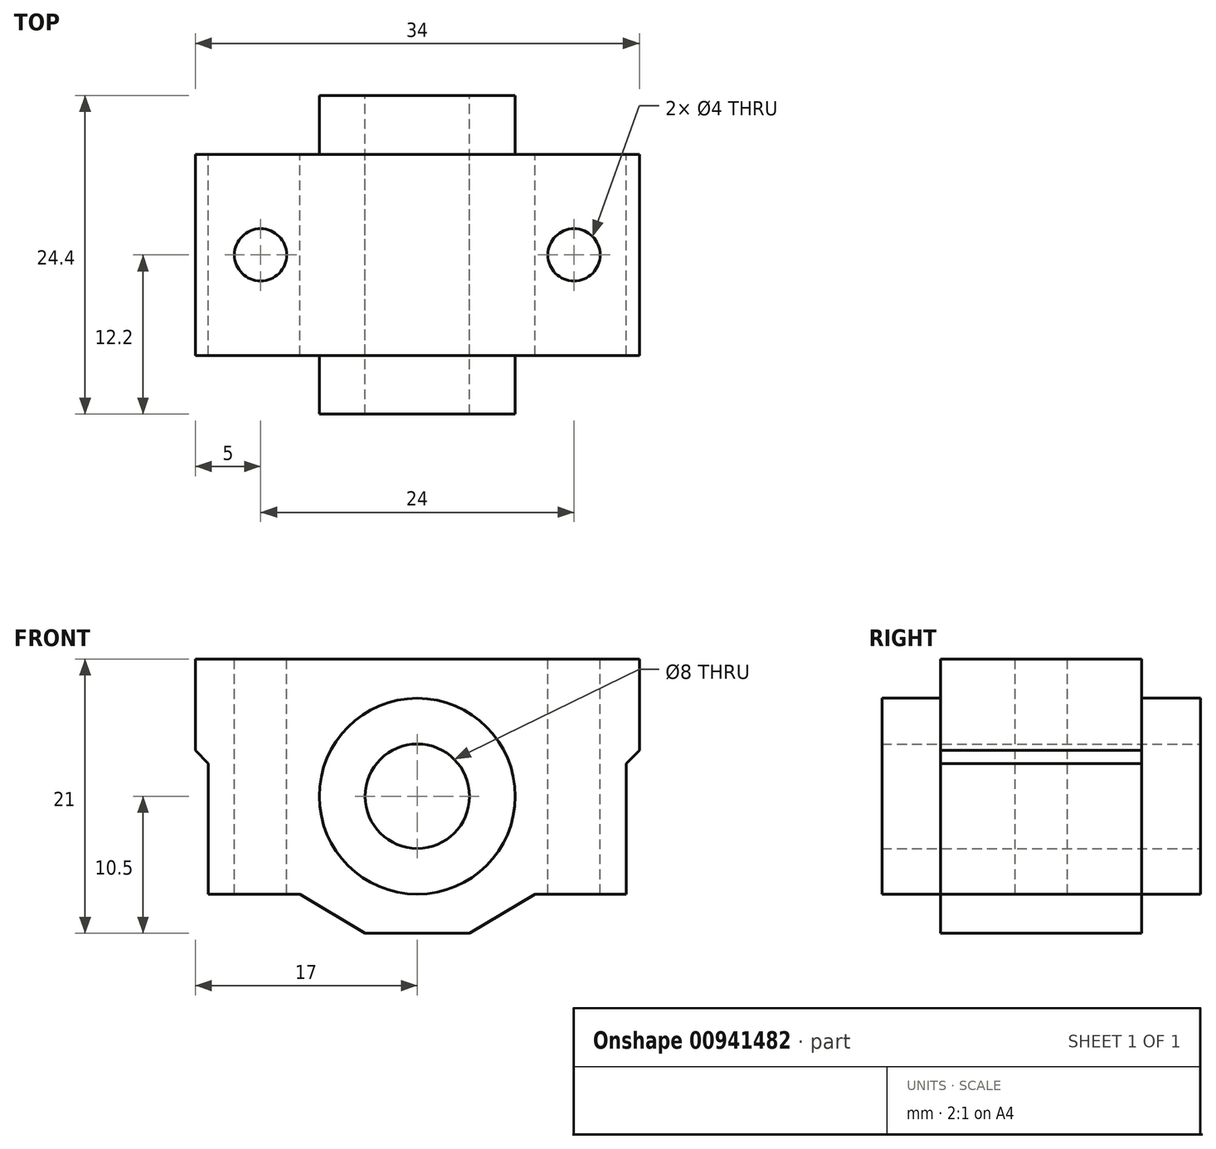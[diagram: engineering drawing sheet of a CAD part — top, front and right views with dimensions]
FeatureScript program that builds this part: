
annotation { "Feature Type Name" : "Feature", "Feature Type Description" : "" }
export const myFeature = defineFeature(function(context is Context, id is Id, definition is map)
    precondition{}
    {
        {
            var Q0;
            Q0=qCreatedBy(makeId("Front.planeOp"),FACE);
            var sketch = newSketch(context, id + "F0", { "sketchPlane" : qUnion([Q0])});
            skLineSegment(sketch, "E0.bottom", {"start": v(4, -10.5) * mm, "end": v(-4, -10.5) * mm});
            skLineSegment(sketch, "E0.top", {"start": v(17, 10.5) * mm, "end": v(-17, 10.5) * mm});
            skLineSegment(sketch, "E0.left", {"start": v(17, 3.5) * mm, "end": v(17, 10.5) * mm});
            skLineSegment(sketch, "E0.right", {"start": v(-17, 3.5) * mm, "end": v(-17, 10.5) * mm});
            skPoint(sketch, "E0.middle", {"position": v(0, 0) * mm});
            skCircle(sketch, "E1", {"center": v(0, 0) * mm, "radius": 7.5 * mm});
            skCircle(sketch, "E2", {"center": v(0, 0) * mm, "radius": 4 * mm});
            skLineSegment(sketch, "E3", {"start": v(16, -7.5) * mm, "end": v(9, -7.5) * mm});
            skLineSegment(sketch, "E4", {"start": v(9, -7.5) * mm, "end": v(4, -10.5) * mm});
            skLineSegment(sketch, "E5", {"start": v(-4, -10.5) * mm, "end": v(-9, -7.5) * mm});
            skLineSegment(sketch, "E6", {"start": v(-9, -7.5) * mm, "end": v(-16, -7.5) * mm});
            skPoint(sketch, "E7.orphan", {"position": v(-17, -10.5) * mm});
            skPoint(sketch, "E8.orphan", {"position": v(17, -10.5) * mm});
            skLineSegment(sketch, "E9", {"start": v(17, 3.5) * mm, "end": v(16, 2.5) * mm});
            skLineSegment(sketch, "E10", {"start": v(16, 2.5) * mm, "end": v(16, -7.5) * mm});
            skLineSegment(sketch, "E11", {"start": v(-17, 3.5) * mm, "end": v(-16, 2.5) * mm});
            skLineSegment(sketch, "E12", {"start": v(-16, 2.5) * mm, "end": v(-16, -7.5) * mm});
            skPoint(sketch, "E13.orphan", {"position": v(-17, -7.5) * mm});
            skPoint(sketch, "E14.orphan", {"position": v(17, -7.5) * mm});
            skSolve(sketch);
        }
        {
            var Q0;
            Q0=makeQuery(id+"F0.imprint","IMPRINT",FACE,{"disambiguationData":[TD([[makeQuery(id+"F0.imprint","IMPRINT",EDGE,{"derivedFrom":sQuery(id+"F0.wireOp",EDGE,"E0.top")}),1.0]])]});
            extrude(context, id + "F1", {"entities" : qUnion([Q0]), "depth" : 7.7 * mm, "offsetDistance" : 25 * mm, "hasSecondDirection" : true, "secondDirectionOppositeDirection" : true, "secondDirectionDepth" : 7.7 * mm});
        }
        {
            var Q0;
            Q0=makeQuery(id+"F1.opExtrude","SWEPT_FACE",FACE,{"disambiguationData":[OSD([sQuery(id+"F0.wireOp",EDGE,"E0.top")])]});
            var sketch = newSketch(context, id + "F2", { "sketchPlane" : qUnion([Q0])});
            skCircle(sketch, "E15", {"center": v(-12, 0) * mm, "radius": 2 * mm});
            skCircle(sketch, "E16", {"center": v(12, 0) * mm, "radius": 2 * mm});
            skSolve(sketch);
        }
        {
            var Q0;
            Q0=makeQuery(id+"F2.imprint","IMPRINT",FACE,{"disambiguationData":[TD([[makeQuery(id+"F2.imprint","IMPRINT",EDGE,{"derivedFrom":sQuery(id+"F2.wireOp",EDGE,"E15")}),1.0]])]});
            var Q1;
            Q1=makeQuery(id+"F2.imprint","IMPRINT",FACE,{"disambiguationData":[TD([[makeQuery(id+"F2.imprint","IMPRINT",EDGE,{"derivedFrom":sQuery(id+"F2.wireOp",EDGE,"E16")}),1.0]])]});
            extrude(context, id + "F3", {"entities" : qUnion([Q0, Q1]), "operationType" : NewBodyOperationType.REMOVE, "oppositeDirection" : true, "depth" : 25 * mm, "offsetDistance" : 25 * mm});
        }
        {
            var Q0;
            Q0=qCreatedBy(makeId("Front.planeOp"),FACE);
            var sketch = newSketch(context, id + "F4", { "sketchPlane" : qUnion([Q0])});
            skCircle(sketch, "E17", {"center": v(0, 0) * mm, "radius": 7.5 * mm});
            skCircle(sketch, "E18", {"center": v(0, 0) * mm, "radius": 4 * mm});
            skSolve(sketch);
        }
        {
            var Q0;
            Q0=makeQuery(id+"F4.imprint","IMPRINT",FACE,{"disambiguationData":[TD([[makeQuery(id+"F4.imprint","IMPRINT",EDGE,{"derivedFrom":sQuery(id+"F4.wireOp",EDGE,"E17")}),1.0]])]});
            extrude(context, id + "F5", {"entities" : qUnion([Q0]), "operationType" : NewBodyOperationType.ADD, "depth" : 12.2 * mm, "offsetDistance" : 25 * mm, "hasSecondDirection" : true, "secondDirectionOppositeDirection" : true, "secondDirectionDepth" : 12.2 * mm});
        }
    });
